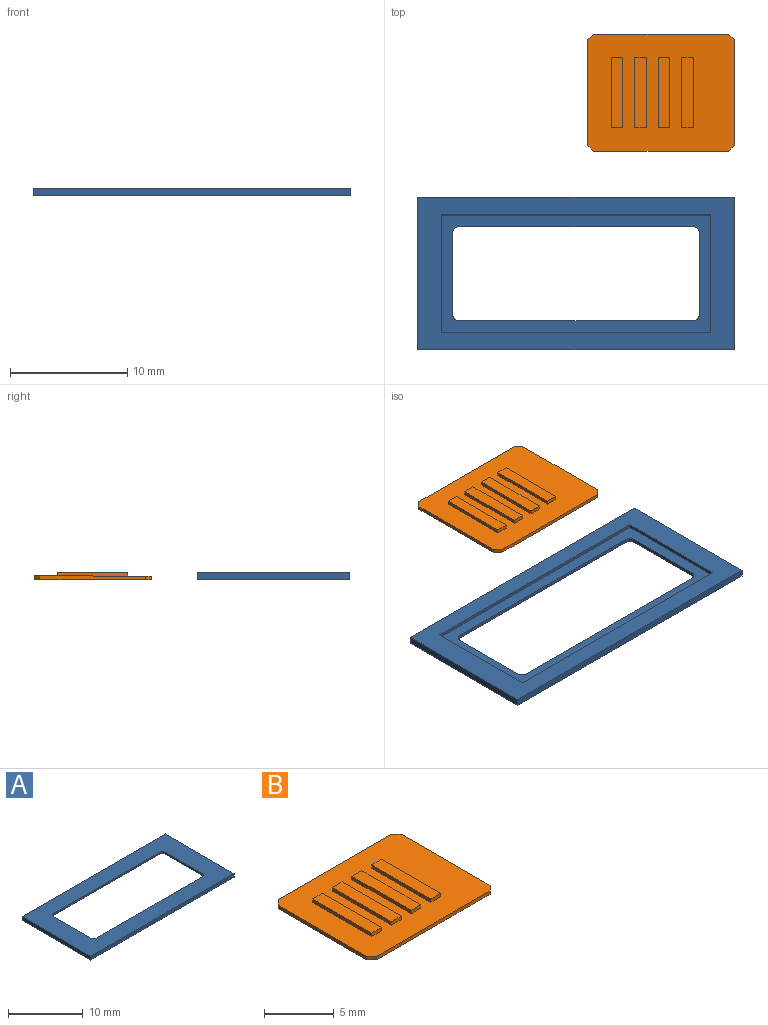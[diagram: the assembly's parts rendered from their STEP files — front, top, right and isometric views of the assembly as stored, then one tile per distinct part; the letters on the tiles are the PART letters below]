
ASSEMBLY  parts=2 mates=2
PART A: 19 faces, bbox 27x13x0.6 mm
  f0: plane 23x10mm, normal (0,0,-1), area 62.2mm2, adj f1,f2,f3,f8,f10,f11,f12,f13
  f1: plane 7x0.3mm, normal (1,0,0), area 2.1mm2, adj f0,f9,f15,f18
  f2: plane 20x0.3mm, normal (0,-1,0), area 6mm2, adj f0,f9,f15,f16
  f3: plane 7x0.3mm, normal (-1,0,0), area 2.1mm2, adj f0,f9,f16,f17
  f4: plane 27x0.6mm, normal (0,1,0), area 16.2mm2, adj f5,f7,f9,f14
  f5: plane 13x0.6mm, normal (-1,0,0), area 7.8mm2, adj f4,f6,f9,f14
  f6: plane 27x0.6mm, normal (0,-1,0), area 16.2mm2, adj f5,f7,f9,f14
  f7: plane 13x0.6mm, normal (1,0,0), area 7.8mm2, adj f4,f6,f9,f14
  f8: plane 20x0.3mm, normal (0,1,0), area 6mm2, adj f0,f9,f17,f18
  f9: plane 27x13mm, normal (0,0,1), area 183.2mm2, adj f1,f2,f3,f4,f5,f6,f7,f8
  f10: plane 10x0.3mm, normal (1,0,0), area 3mm2, adj f0,f11,f13,f14
  f11: plane 23x0.3mm, normal (0,-1,0), area 6.9mm2, adj f0,f10,f12,f14
  f12: plane 10x0.3mm, normal (-1,0,0), area 3mm2, adj f0,f11,f13,f14
  f13: plane 23x0.3mm, normal (0,1,0), area 6.9mm2, adj f0,f10,f12,f14
  f14: plane 27x13mm, normal (0,0,-1), area 121mm2, adj f4,f5,f6,f7,f10,f11,f12,f13
  f15: cylinder r=0.5mm len=0.5mm, axis (0,0,1), area 0.2mm2, adj f0,f1,f2,f9
  f16: cylinder r=0.5mm len=0.5mm, axis (0,0,-1), area 0.2mm2, adj f0,f2,f3,f9
  f17: cylinder r=0.5mm len=0.5mm, axis (0,0,1), area 0.2mm2, adj f0,f3,f8,f9
  f18: cylinder r=0.5mm len=0.5mm, axis (0,0,-1), area 0.2mm2, adj f0,f1,f8,f9
PART B: 30 faces, bbox 12.5x10x0.6 mm
  f0: plane 12.5x10mm, normal (0,0,1), area 100.5mm2, adj f1,f2,f3,f4,f6,f7,f8,f9
  f1: plane 1x0.3mm, normal (0,1,0), area 0.3mm2, adj f0,f2,f4,f5
  f2: plane 6x0.3mm, normal (-1,0,0), area 1.8mm2, adj f0,f1,f3,f5
  f3: plane 1x0.3mm, normal (0,-1,0), area 0.3mm2, adj f0,f2,f4,f5
  f4: plane 6x0.3mm, normal (1,0,0), area 1.8mm2, adj f0,f1,f3,f5
  f5: plane 6x1mm, normal (0,0,1), area 6mm2, adj f1,f2,f3,f4
  f6: plane 9x0.3mm, normal (-1,0,0), area 2.7mm2, adj f0,f10,f26,f27
  f7: plane 11.5x0.3mm, normal (0,1,0), area 3.4mm2, adj f0,f10,f26,f28
  f8: plane 9x0.3mm, normal (1,0,0), area 2.7mm2, adj f0,f10,f28,f29
  f9: plane 11.5x0.3mm, normal (0,-1,0), area 3.4mm2, adj f0,f10,f27,f29
  f10: plane 12.5x10mm, normal (0,0,-1), area 124.5mm2, adj f6,f7,f8,f9,f26,f27,f28,f29
  f11: plane 1x0.3mm, normal (0,1,0), area 0.3mm2, adj f0,f12,f14,f15
  f12: plane 6x0.3mm, normal (-1,0,0), area 1.8mm2, adj f0,f11,f13,f15
  f13: plane 1x0.3mm, normal (0,-1,0), area 0.3mm2, adj f0,f12,f14,f15
  f14: plane 6x0.3mm, normal (1,0,0), area 1.8mm2, adj f0,f11,f13,f15
  f15: plane 6x1mm, normal (0,0,1), area 6mm2, adj f11,f12,f13,f14
  f16: plane 1x0.3mm, normal (0,1,0), area 0.3mm2, adj f0,f17,f19,f20
  f17: plane 6x0.3mm, normal (-1,0,0), area 1.8mm2, adj f0,f16,f18,f20
  f18: plane 1x0.3mm, normal (0,-1,0), area 0.3mm2, adj f0,f17,f19,f20
  f19: plane 6x0.3mm, normal (1,0,0), area 1.8mm2, adj f0,f16,f18,f20
  f20: plane 6x1mm, normal (0,0,1), area 6mm2, adj f16,f17,f18,f19
  f21: plane 1x0.3mm, normal (0,1,0), area 0.3mm2, adj f0,f22,f24,f25
  f22: plane 6x0.3mm, normal (-1,0,0), area 1.8mm2, adj f0,f21,f23,f25
  f23: plane 1x0.3mm, normal (0,-1,0), area 0.3mm2, adj f0,f22,f24,f25
  f24: plane 6x0.3mm, normal (1,0,0), area 1.8mm2, adj f0,f21,f23,f25
  f25: plane 6x1mm, normal (0,0,1), area 6mm2, adj f21,f22,f23,f24
  f26: plane 0.5x0.5mm, normal (-0.71,0.71,0), area 0.2mm2, adj f0,f6,f7,f10
  f27: plane 0.5x0.5mm, normal (-0.71,-0.71,0), area 0.2mm2, adj f0,f6,f9,f10
  f28: plane 0.5x0.5mm, normal (0.71,0.71,0), area 0.2mm2, adj f0,f7,f8,f10
  f29: plane 0.5x0.5mm, normal (0.71,-0.71,0), area 0.2mm2, adj f0,f8,f9,f10
PLACE A rot(axis=(1,0,0),180deg) t=(-13.5,-6.5,0)mm
PLACE B t=(-1,8.92,0.6)mm
MATE planar A.f7 <-> B.f8  axis (1,0,0) through (0,-6.5,0.3)mm
MATE planar B.f10 <-> A.f9  axis (0,0,-1) through (-6.25,8.92,0)mm
